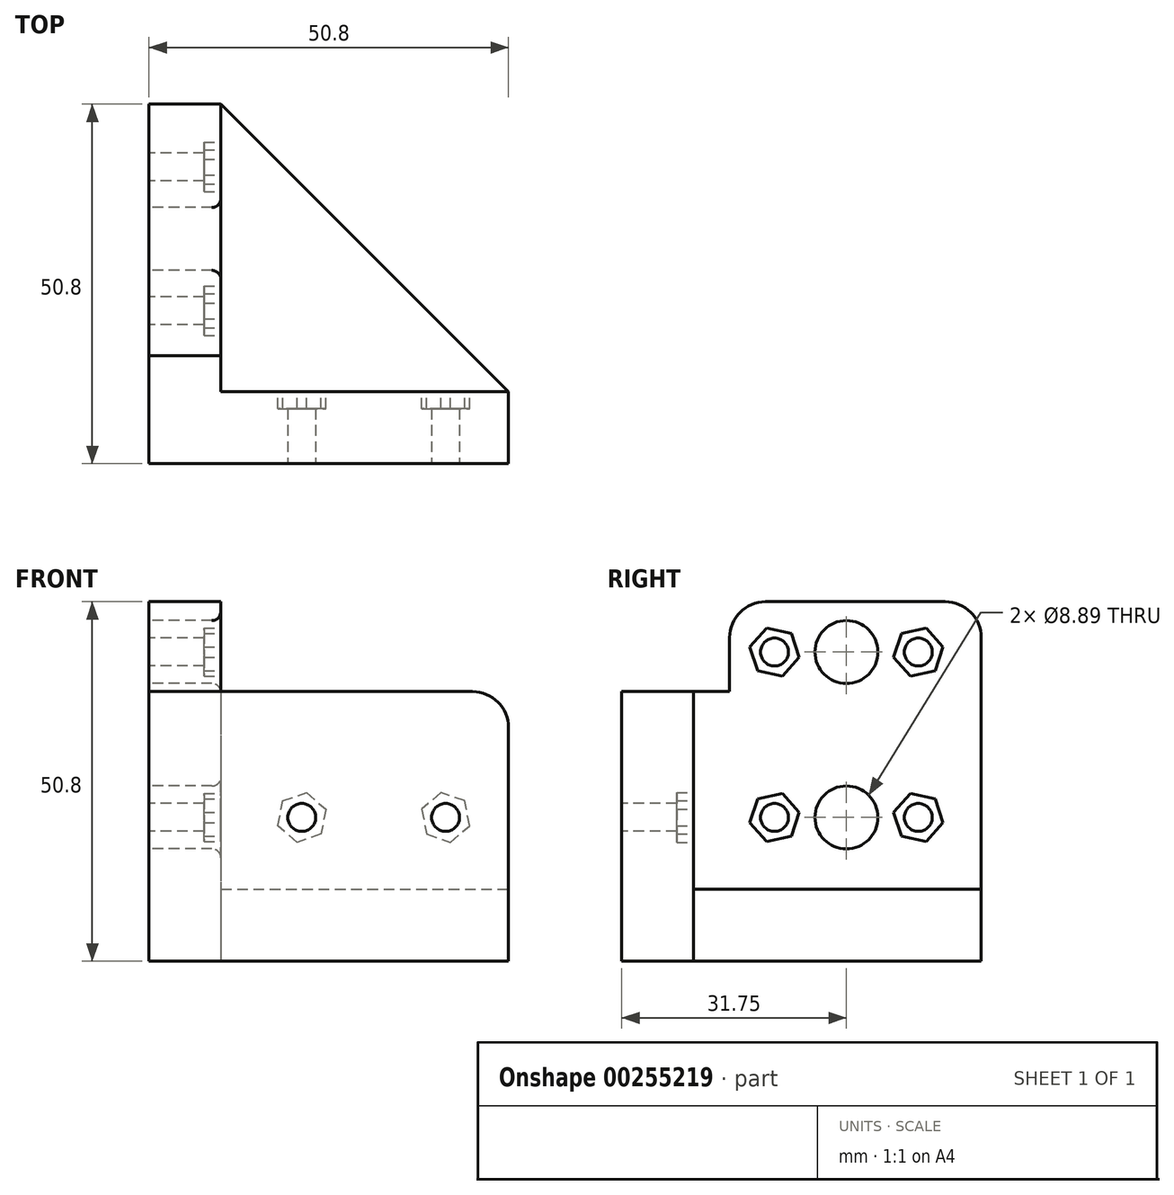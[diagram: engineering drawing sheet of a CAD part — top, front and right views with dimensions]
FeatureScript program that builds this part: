
annotation { "Feature Type Name" : "Feature", "Feature Type Description" : "" }
export const myFeature = defineFeature(function(context is Context, id is Id, definition is map)
    precondition{}
    {
        {
            var Q0;
            Q0=qCreatedBy(makeId("Right.planeOp"),FACE);
            var sketch = newSketch(context, id + "F0", { "sketchPlane" : qUnion([Q0])});
            skLineSegment(sketch, "E0", {"start": v(0, 50.8) * mm, "end": v(0, 0) * mm});
            skCircle(sketch, "E1", {"center": v(31.75, 43.69) * mm, "radius": 4.45 * mm});
            skCircle(sketch, "E2", {"center": v(21.59, 43.69) * mm, "radius": 1.97 * mm});
            skLineSegment(sketch, "E3", {"start": v(31.75, 50.8) * mm, "end": v(31.75, 0) * mm, "construction": true});
            skCircle(sketch, "E4.MirrorC", {"center": v(41.91, 43.69) * mm, "radius": 1.97 * mm});
            skLineSegment(sketch, "E5", {"start": v(31.75, 0) * mm, "end": v(31.75, 20.32) * mm});
            skCircle(sketch, "E6", {"center": v(31.75, 20.32) * mm, "radius": 4.45 * mm});
            skLineSegment(sketch, "E7", {"start": v(33.02, 32) * mm, "end": v(83.82, 32) * mm, "construction": true});
            skCircle(sketch, "E8.MirrorC", {"center": v(41.91, 20.32) * mm, "radius": 1.97 * mm});
            skCircle(sketch, "E9.MirrorC", {"center": v(21.59, 20.32) * mm, "radius": 1.97 * mm});
            skLineSegment(sketch, "E10", {"start": v(0, 50.8) * mm, "end": v(50.8, 50.8) * mm});
            skLineSegment(sketch, "E11", {"start": v(50.8, 50.8) * mm, "end": v(50.8, 0) * mm});
            skLineSegment(sketch, "E12", {"start": v(50.8, 0) * mm, "end": v(0, 0) * mm});
            skLineSegment(sketch, "E13", {"start": v(31.75, 50.8) * mm, "end": v(21.59, 50.8) * mm});
            skLineSegment(sketch, "E14", {"start": v(21.59, 50.8) * mm, "end": v(21.59, 43.69) * mm});
            skLineSegment(sketch, "E15", {"start": v(0, 50.8) * mm, "end": v(15.24, 50.8) * mm});
            skLineSegment(sketch, "E16", {"start": v(15.24, 50.8) * mm, "end": v(15.24, 38.1) * mm});
            skLineSegment(sketch, "E17", {"start": v(15.24, 38.1) * mm, "end": v(0, 38.1) * mm});
            skSolve(sketch);
        }
        {
            var Q0;
            {var subQ3=sQuery(id+"F0.wireOp",EDGE,"bK2mGK6n-yJok-had9-rEAc-foUIrnLmBxiH");Q0=makeQuery(id+"F0.imprint","IMPRINT",FACE,{"disambiguationData":[TD([[makeQuery(id+"F0.imprint","IMPRINT",EDGE,{"derivedFrom":subQ3}),1.0]])]});}
            var Q1;
            Q1=makeQuery(id+"F0.imprint","IMPRINT",FACE,{"disambiguationData":[TD([[makeQuery(id+"F0.imprint","IMPRINT",EDGE,{"derivedFrom":sQuery(id+"F0.wireOp",EDGE,"E6")}),-1.0]])]});
            var Q2;
            {var subQ6=sQuery(id+"F0.wireOp",EDGE,"iSvcAqRB-OP4Y-MQGi-EdqJ-VCbzYJUOz1HD");Q2=makeQuery(id+"F0.imprint","IMPRINT",FACE,{"disambiguationData":[TD([[makeQuery(id+"F0.imprint","IMPRINT",EDGE,{"derivedFrom":subQ6}),-1.0]])]});}
            extrude(context, id + "F1", {"entities" : qUnion([Q0, Q1, Q2]), "depth" : 10.16 * mm});
        }
        {
            var Q0;
            Q0=makeQuery(id+"F1.opExtrude","CAP_FACE",FACE,{"disambiguationData":[OSD([sQuery(id+"F0.wireOp",EDGE,"E0"),sQuery(id+"F0.wireOp",EDGE,"E1"),sQuery(id+"F0.wireOp",EDGE,"E2"),sQuery(id+"F0.wireOp",EDGE,"E4.MirrorC"),sQuery(id+"F0.wireOp",EDGE,"E6"),sQuery(id+"F0.wireOp",EDGE,"E8.MirrorC"),sQuery(id+"F0.wireOp",EDGE,"E9.MirrorC"),sQuery(id+"F0.wireOp",EDGE,"E10"),sQuery(id+"F0.wireOp",EDGE,"E11"),sQuery(id+"F0.wireOp",EDGE,"E12"),sQuery(id+"F0.wireOp",EDGE,"E13")])],"isStart":false});
            var sketch = newSketch(context, id + "F2", { "sketchPlane" : qUnion([Q0])});
            skLineSegment(sketch, "E18", {"start": v(21.59, 43.69) * mm, "end": v(21.59, 20.32) * mm, "construction": true});
            skLineSegment(sketch, "E19", {"start": v(21.59, 20.32) * mm, "end": v(41.91, 20.32) * mm, "construction": true});
            skLineSegment(sketch, "E20", {"start": v(41.91, 20.32) * mm, "end": v(41.91, 43.69) * mm, "construction": true});
            skLineSegment(sketch, "E21", {"start": v(41.91, 43.69) * mm, "end": v(21.59, 43.69) * mm, "construction": true});
            skLineSegment(sketch, "E22", {"start": v(31.75, 43.69) * mm, "end": v(31.75, 20.32) * mm, "construction": true});
            skLineSegment(sketch, "E23", {"start": v(21.59, 32) * mm, "end": v(41.91, 32) * mm, "construction": true});
            skCircle(sketch, "E24.cCircle", {"center": v(21.59, 43.69) * mm, "radius": 3.1 * mm, "construction": true});
            skLineSegment(sketch, "E24.0", {"start": v(18.1, 44.44) * mm, "end": v(20.5, 47.1) * mm});
            skLineSegment(sketch, "E24.1", {"start": v(20.5, 47.1) * mm, "end": v(24, 46.34) * mm});
            skLineSegment(sketch, "E24.2", {"start": v(24, 46.34) * mm, "end": v(25.09, 42.94) * mm});
            skLineSegment(sketch, "E24.3", {"start": v(25.09, 42.94) * mm, "end": v(22.69, 40.28) * mm});
            skLineSegment(sketch, "E24.4", {"start": v(22.69, 40.28) * mm, "end": v(19.19, 41.03) * mm});
            skLineSegment(sketch, "E24.5", {"start": v(19.19, 41.03) * mm, "end": v(18.1, 44.44) * mm});
            skPoint(sketch, "E24.0.midPoint", {"position": v(19.3, 45.77) * mm});
            skPoint(sketch, "E25.MirrorP", {"position": v(44.2, 45.77) * mm});
            skLineSegment(sketch, "E26.MirrorCS", {"start": v(44.31, 41.03) * mm, "end": v(45.4, 44.44) * mm});
            skLineSegment(sketch, "E27.MirrorCS", {"start": v(43, 47.1) * mm, "end": v(39.5, 46.34) * mm});
            skLineSegment(sketch, "E28.MirrorCS", {"start": v(39.5, 46.34) * mm, "end": v(38.41, 42.94) * mm});
            skLineSegment(sketch, "E29.MirrorCS", {"start": v(38.41, 42.94) * mm, "end": v(40.81, 40.28) * mm});
            skLineSegment(sketch, "E30.MirrorCS", {"start": v(40.81, 40.28) * mm, "end": v(44.31, 41.03) * mm});
            skCircle(sketch, "E31.MirrorC", {"center": v(41.91, 43.69) * mm, "radius": 3.1 * mm, "construction": true});
            skLineSegment(sketch, "E32.MirrorCS", {"start": v(45.4, 44.44) * mm, "end": v(43, 47.1) * mm});
            skLineSegment(sketch, "E33.MirrorCS", {"start": v(40.81, 23.73) * mm, "end": v(44.31, 22.97) * mm});
            skLineSegment(sketch, "E34.MirrorCS", {"start": v(43, 16.91) * mm, "end": v(39.5, 17.67) * mm});
            skLineSegment(sketch, "E35.MirrorCS", {"start": v(44.31, 22.97) * mm, "end": v(45.4, 19.57) * mm});
            skLineSegment(sketch, "E36.MirrorCS", {"start": v(45.4, 19.57) * mm, "end": v(43, 16.91) * mm});
            skLineSegment(sketch, "E37.MirrorCS", {"start": v(38.41, 21.07) * mm, "end": v(40.81, 23.73) * mm});
            skCircle(sketch, "E38.MirrorC", {"center": v(41.91, 20.32) * mm, "radius": 3.1 * mm, "construction": true});
            skPoint(sketch, "E39.MirrorP", {"position": v(44.2, 18.24) * mm});
            skLineSegment(sketch, "E40.MirrorCS", {"start": v(39.5, 17.67) * mm, "end": v(38.41, 21.07) * mm});
            skPoint(sketch, "E41.MirrorP", {"position": v(19.3, 18.24) * mm});
            skLineSegment(sketch, "E42.MirrorCS", {"start": v(19.19, 22.97) * mm, "end": v(18.1, 19.57) * mm});
            skLineSegment(sketch, "E43.MirrorCS", {"start": v(22.69, 23.73) * mm, "end": v(19.19, 22.97) * mm});
            skLineSegment(sketch, "E44.MirrorCS", {"start": v(25.09, 21.07) * mm, "end": v(22.69, 23.73) * mm});
            skLineSegment(sketch, "E45.MirrorCS", {"start": v(24, 17.67) * mm, "end": v(25.09, 21.07) * mm});
            skLineSegment(sketch, "E46.MirrorCS", {"start": v(18.1, 19.57) * mm, "end": v(20.5, 16.91) * mm});
            skLineSegment(sketch, "E47.MirrorCS", {"start": v(20.5, 16.91) * mm, "end": v(24, 17.67) * mm});
            skCircle(sketch, "E48.MirrorC", {"center": v(21.59, 20.32) * mm, "radius": 3.1 * mm, "construction": true});
            skSolve(sketch);
        }
        {
            var Q0;
            Q0=makeQuery(id+"F2.imprint","IMPRINT",FACE,{"disambiguationData":[TD([[makeQuery(id+"F2.imprint","IMPRINT",EDGE,{"derivedFrom":sQuery(id+"F2.wireOp",EDGE,"E24.0")}),-1.0]])]});
            var Q1;
            Q1=makeQuery(id+"F2.imprint","IMPRINT",FACE,{"disambiguationData":[TD([[makeQuery(id+"F2.imprint","IMPRINT",EDGE,{"derivedFrom":sQuery(id+"F2.wireOp",EDGE,"E26.MirrorCS")}),1.0]])]});
            var Q2;
            Q2=makeQuery(id+"F2.imprint","IMPRINT",FACE,{"disambiguationData":[TD([[makeQuery(id+"F2.imprint","IMPRINT",EDGE,{"derivedFrom":sQuery(id+"F2.wireOp",EDGE,"E33.MirrorCS")}),-1.0]])]});
            var Q3;
            Q3=makeQuery(id+"F2.imprint","IMPRINT",FACE,{"disambiguationData":[TD([[makeQuery(id+"F2.imprint","IMPRINT",EDGE,{"derivedFrom":sQuery(id+"F2.wireOp",EDGE,"E42.MirrorCS")}),1.0]])]});
            extrude(context, id + "F3", {"entities" : qUnion([Q0, Q1, Q2, Q3]), "operationType" : NewBodyOperationType.REMOVE, "oppositeDirection" : true, "depth" : 2.4 * mm});
        }
        {
            var Q0;
            Q0=makeQuery(id+"Fgkhg6nh0ea1WLk_1.opPattern","COPY",EDGE,{"derivedFrom":makeQuery(id+"F1.opExtrude","SWEPT_EDGE",EDGE,{"disambiguationData":[OSD([sQuery(id+"F0.wireOp",EDGE,"E10"),sQuery(id+"F0.wireOp",EDGE,"E11")])]}),"instanceName":"1"});
            var Q1;
            Q1=makeQuery(id+"F1.opExtrude","SWEPT_EDGE",EDGE,{"disambiguationData":[OSD([sQuery(id+"F0.wireOp",EDGE,"E10"),sQuery(id+"F0.wireOp",EDGE,"E11")])]});
            var Q2;
            {var subQ0=sQuery(id+"FfOvtivRF5K7VSy_1.wireOp",EDGE,"jhL4Jv3K-tLSI-RbRH-XfF7-147F2JV6tCMN");Q2=makeQuery(id+"FzIobM9Km7jxFAJ_1.opChamfer","BLEND_EDGE",EDGE,{"blendedFrom":[makeQuery(id+"FN15cnjGST75Ql2_1.opExtrude","CAP_EDGE",EDGE,{"disambiguationData":[OSD([subQ0])],"isStart":false}),makeQuery(id+"FN15cnjGST75Ql2_1.boolean.opBoolean","MERGE",FACE,{"derivedFrom":[makeQuery(id+"Fgkhg6nh0ea1WLk_1.opPattern","COPY",FACE,{"derivedFrom":makeQuery(id+"F1.opExtrude","SWEPT_FACE",FACE,{"disambiguationData":[OSD([sQuery(id+"F0.wireOp",EDGE,"E11")])]}),"instanceName":"1"}),makeQuery(id+"FN15cnjGST75Ql2_1.opExtrude","CAP_FACE",FACE,{"disambiguationData":[OSD([subQ0,sQuery(id+"FfOvtivRF5K7VSy_1.wireOp",EDGE,"5yxtnuUS-IApM-TYjR-IxmS-DzZvyduIwBBn"),sQuery(id+"FfOvtivRF5K7VSy_1.wireOp",EDGE,"VCPRvI0m-5Ndb-sGlJ-Yh6E-NNUC6tKog5Ip"),sQuery(id+"FfOvtivRF5K7VSy_1.wireOp",EDGE,"2WnT3rEx-PQ5a-MxGm-VFJZ-yFCLeYtDUc3R")])],"isStart":false})]})],"blendedInto":[makeQuery(id+"FN15cnjGST75Ql2_1.boolean.opBoolean","MERGE",FACE,{"derivedFrom":[makeQuery(id+"Fgkhg6nh0ea1WLk_1.opPattern","COPY",FACE,{"derivedFrom":makeQuery(id+"F1.opExtrude","SWEPT_FACE",FACE,{"disambiguationData":[OSD([sQuery(id+"F0.wireOp",EDGE,"E11")])]}),"instanceName":"1"}),makeQuery(id+"FN15cnjGST75Ql2_1.opExtrude","CAP_FACE",FACE,{"disambiguationData":[OSD([subQ0,sQuery(id+"FfOvtivRF5K7VSy_1.wireOp",EDGE,"5yxtnuUS-IApM-TYjR-IxmS-DzZvyduIwBBn"),sQuery(id+"FfOvtivRF5K7VSy_1.wireOp",EDGE,"VCPRvI0m-5Ndb-sGlJ-Yh6E-NNUC6tKog5Ip"),sQuery(id+"FfOvtivRF5K7VSy_1.wireOp",EDGE,"2WnT3rEx-PQ5a-MxGm-VFJZ-yFCLeYtDUc3R")])],"isStart":false})]})]});}
            var Q3;
            {var subQ0=sQuery(id+"FfOvtivRF5K7VSy_1.wireOp",EDGE,"jhL4Jv3K-tLSI-RbRH-XfF7-147F2JV6tCMN");Q3=makeQuery(id+"FzIobM9Km7jxFAJ_1.opChamfer","BLEND_EDGE",EDGE,{"blendedFrom":[makeQuery(id+"FN15cnjGST75Ql2_1.opExtrude","CAP_EDGE",EDGE,{"disambiguationData":[OSD([subQ0])],"isStart":false}),makeQuery(id+"FN15cnjGST75Ql2_1.boolean.opBoolean","MERGE",FACE,{"derivedFrom":[makeQuery(id+"F1.opExtrude","SWEPT_FACE",FACE,{"disambiguationData":[OSD([sQuery(id+"F0.wireOp",EDGE,"E11")])]}),makeQuery(id+"FN15cnjGST75Ql2_1.opExtrude","SWEPT_FACE",FACE,{"disambiguationData":[OSD([subQ0])]})]})],"blendedInto":[makeQuery(id+"FN15cnjGST75Ql2_1.boolean.opBoolean","MERGE",FACE,{"derivedFrom":[makeQuery(id+"F1.opExtrude","SWEPT_FACE",FACE,{"disambiguationData":[OSD([sQuery(id+"F0.wireOp",EDGE,"E11")])]}),makeQuery(id+"FN15cnjGST75Ql2_1.opExtrude","SWEPT_FACE",FACE,{"disambiguationData":[OSD([subQ0])]})]})]});}
            fillet(context, id + "F4", {"entities" : qUnion([Q0, Q1, Q2, Q3]), "radius" : 5.08 * mm, "tangentPropagation" : true, "allowEdgeOverflow" : false});
        }
        {
            var Q0;
            Q0=qCreatedBy(makeId("Front.planeOp"),FACE);
            var sketch = newSketch(context, id + "F5", { "sketchPlane" : qUnion([Q0])});
            skLineSegment(sketch, "E49", {"start": v(0, 0) * mm, "end": v(50.8, 0) * mm});
            skLineSegment(sketch, "E50", {"start": v(0, 0) * mm, "end": v(0, 38.1) * mm});
            skLineSegment(sketch, "E51", {"start": v(0, 38.1) * mm, "end": v(50.8, 38.1) * mm});
            skLineSegment(sketch, "E52", {"start": v(50.8, 38.1) * mm, "end": v(50.8, 0) * mm});
            skLineSegment(sketch, "E53", {"start": v(31.75, 38.1) * mm, "end": v(31.75, 0) * mm, "construction": true});
            skLineSegment(sketch, "E54", {"start": v(50.8, 20.32) * mm, "end": v(0, 20.32) * mm, "construction": true});
            skCircle(sketch, "E55", {"center": v(41.91, 20.32) * mm, "radius": 1.97 * mm});
            skCircle(sketch, "E56.MirrorC", {"center": v(21.6, 20.32) * mm, "radius": 1.97 * mm});
            skSolve(sketch);
        }
        {
            var Q0;
            Q0=makeQuery(id+"F5.imprint","IMPRINT",FACE,{"disambiguationData":[TD([[makeQuery(id+"F5.imprint","IMPRINT",EDGE,{"derivedFrom":sQuery(id+"F5.wireOp",EDGE,"E49")}),1.0]])]});
            extrude(context, id + "F6", {"entities" : qUnion([Q0]), "operationType" : NewBodyOperationType.ADD, "oppositeDirection" : true, "depth" : 10.16 * mm});
        }
        {
            var Q0;
            Q0=makeQuery(id+"F6.opExtrude","SWEPT_EDGE",EDGE,{"disambiguationData":[OSD([sQuery(id+"F5.wireOp",EDGE,"E51"),sQuery(id+"F5.wireOp",EDGE,"E52")])]});
            var Q1;
            Q1=makeQuery(id+"F1.opExtrude","SWEPT_EDGE",EDGE,{"disambiguationData":[OSD([sQuery(id+"F0.wireOp",EDGE,"E10"),sQuery(id+"F0.wireOp",EDGE,"E15"),sQuery(id+"F0.wireOp",EDGE,"E16")])]});
            fillet(context, id + "F7", {"entities" : qUnion([Q0, Q1]), "radius" : 5.08 * mm, "tangentPropagation" : true, "allowEdgeOverflow" : false});
        }
        {
            var Q0;
            Q0=makeQuery(id+"F6.opExtrude","CAP_FACE",FACE,{"disambiguationData":[OSD([sQuery(id+"F5.wireOp",EDGE,"E49"),sQuery(id+"F5.wireOp",EDGE,"E50"),sQuery(id+"F5.wireOp",EDGE,"E51"),sQuery(id+"F5.wireOp",EDGE,"E52"),sQuery(id+"F5.wireOp",EDGE,"E55"),sQuery(id+"F5.wireOp",EDGE,"E56.MirrorC")])],"isStart":false});
            var sketch = newSketch(context, id + "F8", { "sketchPlane" : qUnion([Q0])});
            skCircle(sketch, "E57.cCircle", {"center": v(-41.91, 20.32) * mm, "radius": 3.1 * mm, "construction": true});
            skLineSegment(sketch, "E57.0", {"start": v(-44.61, 22.66) * mm, "end": v(-41.23, 23.83) * mm});
            skLineSegment(sketch, "E57.1", {"start": v(-41.23, 23.83) * mm, "end": v(-38.53, 21.49) * mm});
            skLineSegment(sketch, "E57.2", {"start": v(-38.53, 21.49) * mm, "end": v(-39.2, 17.98) * mm});
            skLineSegment(sketch, "E57.3", {"start": v(-39.2, 17.98) * mm, "end": v(-42.59, 16.8) * mm});
            skLineSegment(sketch, "E57.4", {"start": v(-42.59, 16.8) * mm, "end": v(-45.3, 19.15) * mm});
            skLineSegment(sketch, "E57.5", {"start": v(-45.3, 19.15) * mm, "end": v(-44.61, 22.66) * mm});
            skPoint(sketch, "E57.0.midPoint", {"position": v(-42.92, 23.25) * mm});
            skCircle(sketch, "E58.MirrorC", {"center": v(-21.6, 20.32) * mm, "radius": 3.1 * mm, "construction": true});
            skLineSegment(sketch, "E59.MirrorCS", {"start": v(-20.91, 16.8) * mm, "end": v(-18.2, 19.15) * mm});
            skLineSegment(sketch, "E60.MirrorCS", {"start": v(-24.3, 17.98) * mm, "end": v(-20.91, 16.8) * mm});
            skLineSegment(sketch, "E61.MirrorCS", {"start": v(-22.27, 23.83) * mm, "end": v(-24.97, 21.49) * mm});
            skLineSegment(sketch, "E62.MirrorCS", {"start": v(-18.2, 19.15) * mm, "end": v(-18.89, 22.66) * mm});
            skLineSegment(sketch, "E63.MirrorCS", {"start": v(-18.89, 22.66) * mm, "end": v(-22.27, 23.83) * mm});
            skPoint(sketch, "E64.MirrorP", {"position": v(-20.58, 23.25) * mm});
            skLineSegment(sketch, "E65.MirrorCS", {"start": v(-24.97, 21.49) * mm, "end": v(-24.3, 17.98) * mm});
            skSolve(sketch);
        }
        {
            var Q0;
            Q0=makeQuery(id+"F8.imprint","IMPRINT",FACE,{"disambiguationData":[TD([[makeQuery(id+"F8.imprint","IMPRINT",EDGE,{"derivedFrom":sQuery(id+"F8.wireOp",EDGE,"E57.0")}),-1.0]])]});
            var Q1;
            Q1=makeQuery(id+"F8.imprint","IMPRINT",FACE,{"disambiguationData":[TD([[makeQuery(id+"F8.imprint","IMPRINT",EDGE,{"derivedFrom":sQuery(id+"F8.wireOp",EDGE,"E59.MirrorCS")}),1.0]])]});
            extrude(context, id + "F9", {"entities" : qUnion([Q0, Q1]), "operationType" : NewBodyOperationType.REMOVE, "oppositeDirection" : true, "depth" : 2.4 * mm});
        }
        {
            var Q0;
            Q0=makeQuery(id+"F6.boolean.opBoolean","MERGE",FACE,{"derivedFrom":[makeQuery(id+"F1.opExtrude","SWEPT_FACE",FACE,{"disambiguationData":[OSD([sQuery(id+"F0.wireOp",EDGE,"E12")])]}),makeQuery(id+"F6.opExtrude","SWEPT_FACE",FACE,{"disambiguationData":[OSD([sQuery(id+"F5.wireOp",EDGE,"E49")])]})]});
            var sketch = newSketch(context, id + "F10", { "sketchPlane" : qUnion([Q0])});
            skLineSegment(sketch, "E66", {"start": v(10.16, -50.8) * mm, "end": v(50.8, -10.16) * mm});
            skSolve(sketch);
        }
        {
            var Q0;
            Q0=makeQuery(id+"F10.imprint","IMPRINT",FACE,{"disambiguationData":[TD([[makeQuery(id+"F10.imprint","IMPRINT",EDGE,{"derivedFrom":sQuery(id+"F10.wireOp",EDGE,"E66")}),1.0]])]});
            extrude(context, id + "F11", {"entities" : qUnion([Q0]), "oppositeDirection" : true, "depth" : 10.16 * mm});
        }
        {
            var Q0;
            Q0=makeQuery(id+"F1.opExtrude","CAP_EDGE",EDGE,{"disambiguationData":[OSD([sQuery(id+"F0.wireOp",EDGE,"E6")])],"isStart":false});
            var Q1;
            Q1=makeQuery(id+"F1.opExtrude","CAP_EDGE",EDGE,{"disambiguationData":[OSD([sQuery(id+"F0.wireOp",EDGE,"E1")])],"isStart":false});
            fillet(context, id + "F12", {"entities" : qUnion([Q0, Q1]), "radius" : 1.27 * mm, "tangentPropagation" : true, "allowEdgeOverflow" : false});
        }
    });
